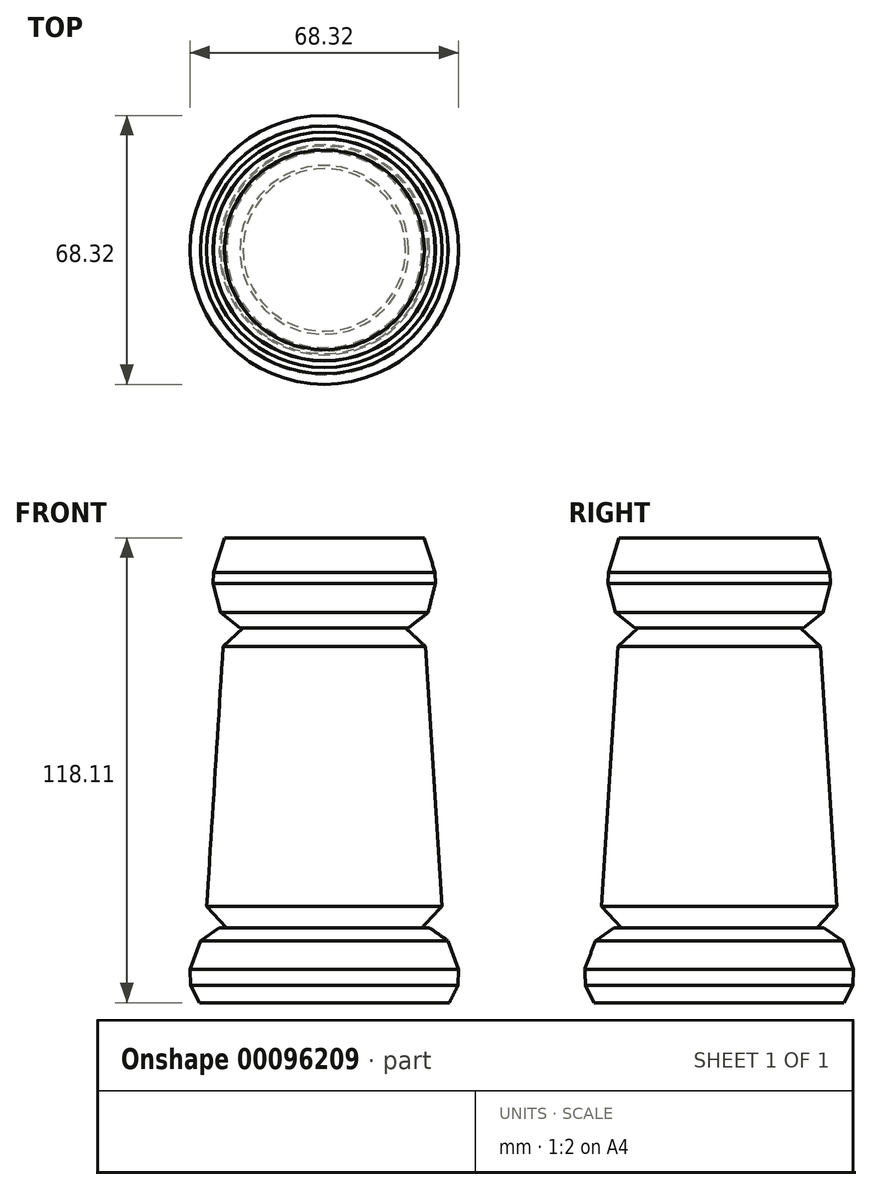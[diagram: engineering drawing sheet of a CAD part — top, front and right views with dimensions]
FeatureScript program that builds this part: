
annotation { "Feature Type Name" : "Feature", "Feature Type Description" : "" }
export const myFeature = defineFeature(function(context is Context, id is Id, definition is map)
    precondition{}
    {
        {
            var Q0;
            Q0=qCreatedBy(makeId("Top.planeOp"),FACE);
            var sketch = newSketch(context, id + "F0", { "sketchPlane" : qUnion([Q0])});
            skCircle(sketch, "E0", {"center": v(0, 0) * mm, "radius": 31.75 * mm});
            skSolve(sketch);
        }
        {
            var Q0;
            Q0=qCreatedBy(makeId("Top.planeOp"),FACE);
            cPlane(context, id + "F1", {"entities" : qUnion([Q0]), "cplaneType" : CPlaneType.OFFSET, "offset" : 6.35 * mm, "width" : 152.4 * mm, "height" : 152.4 * mm});
        }
        {
            var Q0;
            Q0=qCreatedBy(id+"F1.planeOp",FACE);
            var sketch = newSketch(context, id + "F2", { "sketchPlane" : qUnion([Q0])});
            skCircle(sketch, "E1", {"center": v(0, 0) * mm, "radius": 34.92 * mm});
            skSolve(sketch);
        }
        {
            var Q0;
            Q0=makeQuery(id+"F2.imprint","IMPRINT",FACE,{"disambiguationData":[TD([[makeQuery(id+"F2.imprint","IMPRINT",EDGE,{"derivedFrom":sQuery(id+"F2.wireOp",EDGE,"E1")}),1.0]])]});
            var Q1;
            Q1=makeQuery(id+"F0.imprint","IMPRINT",FACE,{"disambiguationData":[TD([[makeQuery(id+"F0.imprint","IMPRINT",EDGE,{"derivedFrom":sQuery(id+"F0.wireOp",EDGE,"E0")}),1.0]])]});
            loft(context, id + "F3", {"sheetProfilesArray" : [{ "sheetProfileEntities" : qUnion([Q0]) }, { "sheetProfileEntities" : qUnion([Q1]) }]});
        }
        {
            var Q0;
            Q0=qCreatedBy(id+"F1.planeOp",FACE);
            cPlane(context, id + "F4", {"entities" : qUnion([Q0]), "cplaneType" : CPlaneType.OFFSET, "offset" : 12.7 * mm, "width" : 152.4 * mm, "height" : 152.4 * mm});
        }
        {
            var Q0;
            Q0=qCreatedBy(id+"F4.planeOp",FACE);
            var sketch = newSketch(context, id + "F5", { "sketchPlane" : qUnion([Q0])});
            skCircle(sketch, "E2", {"center": v(0, 0) * mm, "radius": 30.22 * mm});
            skSolve(sketch);
        }
        {
            var Q1;
            Q1=makeQuery(id+"F5.imprint","IMPRINT",FACE,{"disambiguationData":[TD([[makeQuery(id+"F5.imprint","IMPRINT",EDGE,{"derivedFrom":sQuery(id+"F5.wireOp",EDGE,"E2")}),1.0]])]});
            var Q2;
            Q2=makeQuery(id+"F2.imprint","IMPRINT",FACE,{"disambiguationData":[TD([[makeQuery(id+"F2.imprint","IMPRINT",EDGE,{"derivedFrom":sQuery(id+"F2.wireOp",EDGE,"E1")}),1.0]])]});
            loft(context, id + "F6", {"operationType" : NewBodyOperationType.ADD, "sheetProfilesArray" : [{ "sheetProfileEntities" : qUnion([Q1]) }, { "sheetProfileEntities" : qUnion([Q2]) }]});
        }
        {
            var Q0;
            Q0=qCreatedBy(id+"F4.planeOp",FACE);
            cPlane(context, id + "F7", {"entities" : qUnion([Q0]), "cplaneType" : CPlaneType.OFFSET, "offset" : 76.2 * mm, "width" : 152.4 * mm, "height" : 152.4 * mm});
        }
        {
            var Q0;
            Q0=qCreatedBy(id+"F7.planeOp",FACE);
            var sketch = newSketch(context, id + "F8", { "sketchPlane" : qUnion([Q0])});
            skCircle(sketch, "E3", {"center": v(0, 0) * mm, "radius": 25.4 * mm});
            skSolve(sketch);
        }
        {
            var Q0;
            Q0=qCreatedBy(id+"F7.planeOp",FACE);
            cPlane(context, id + "F9", {"entities" : qUnion([Q0]), "cplaneType" : CPlaneType.OFFSET, "offset" : 12.7 * mm, "width" : 152.4 * mm, "height" : 152.4 * mm});
        }
        {
            var Q0;
            Q0=qCreatedBy(id+"F9.planeOp",FACE);
            var sketch = newSketch(context, id + "F10", { "sketchPlane" : qUnion([Q0])});
            skCircle(sketch, "E4", {"center": v(0, 0) * mm, "radius": 28.58 * mm});
            skSolve(sketch);
        }
        {
            var Q0;
            Q0=makeQuery(id+"F8.imprint","IMPRINT",FACE,{"disambiguationData":[TD([[makeQuery(id+"F8.imprint","IMPRINT",EDGE,{"derivedFrom":sQuery(id+"F8.wireOp",EDGE,"E3")}),1.0]])]});
            var Q1;
            Q1=makeQuery(id+"F10.imprint","IMPRINT",FACE,{"disambiguationData":[TD([[makeQuery(id+"F10.imprint","IMPRINT",EDGE,{"derivedFrom":sQuery(id+"F10.wireOp",EDGE,"E4")}),1.0]])]});
            loft(context, id + "F11", {"sheetProfilesArray" : [{ "sheetProfileEntities" : qUnion([Q0]) }, { "sheetProfileEntities" : qUnion([Q1]) }]});
        }
        {
            var Q0;
            Q0=qCreatedBy(id+"F9.planeOp",FACE);
            cPlane(context, id + "F12", {"entities" : qUnion([Q0]), "cplaneType" : CPlaneType.OFFSET, "offset" : 10.16 * mm, "width" : 152.4 * mm, "height" : 152.4 * mm});
        }
        {
            var Q0;
            Q0=qCreatedBy(id+"F12.planeOp",FACE);
            var sketch = newSketch(context, id + "F13", { "sketchPlane" : qUnion([Q0])});
            skCircle(sketch, "E5", {"center": v(0, 0) * mm, "radius": 25.4 * mm});
            skSolve(sketch);
        }
        {
            var Q0;
            Q0=makeQuery(id+"F6.opLoft","CAP_FACE",FACE,{"disambiguationData":[OSD([makeQuery(id+"F5.imprint","IMPRINT",FACE,{"disambiguationData":[TD([[makeQuery(id+"F5.imprint","IMPRINT",EDGE,{"derivedFrom":sQuery(id+"F5.wireOp",EDGE,"E2")}),1.0]])]})])],"isStart":true});
            var Q1;
            Q1=makeQuery(id+"F11.opLoft","CAP_FACE",FACE,{"disambiguationData":[OSD([makeQuery(id+"F8.imprint","IMPRINT",FACE,{"disambiguationData":[TD([[makeQuery(id+"F8.imprint","IMPRINT",EDGE,{"derivedFrom":sQuery(id+"F8.wireOp",EDGE,"E3")}),1.0]])]})])],"isStart":true});
            loft(context, id + "F14", {"sheetProfilesArray" : [{ "sheetProfileEntities" : qUnion([Q0]) }, { "sheetProfileEntities" : qUnion([Q1]) }]});
        }
        {
            var Q1;
            Q1=makeQuery(id+"F13.imprint","IMPRINT",FACE,{"disambiguationData":[TD([[makeQuery(id+"F13.imprint","IMPRINT",EDGE,{"derivedFrom":sQuery(id+"F13.wireOp",EDGE,"E5")}),1.0]])]});
            var Q2;
            Q2=makeQuery(id+"F11.opLoft","CAP_FACE",FACE,{"disambiguationData":[OSD([makeQuery(id+"F10.imprint","IMPRINT",FACE,{"disambiguationData":[TD([[makeQuery(id+"F10.imprint","IMPRINT",EDGE,{"derivedFrom":sQuery(id+"F10.wireOp",EDGE,"E4")}),1.0]])]})])],"isStart":true});
            loft(context, id + "F15", {"operationType" : NewBodyOperationType.ADD, "sheetProfilesArray" : [{ "sheetProfileEntities" : qUnion([Q1]) }, { "sheetProfileEntities" : qUnion([Q2]) }]});
        }
        {
            var Q0;
            Q0=makeQuery(id+"F14.opLoft","SWEPT_FACE",FACE,{"disambiguationData":[OSD([sQuery(id+"F5.wireOp",EDGE,"E2"),sQuery(id+"F8.wireOp",EDGE,"E3")])]});
            var Q1;
            Q1=makeQuery(id+"F6.opLoft","SWEPT_FACE",FACE,{"disambiguationData":[OSD([sQuery(id+"F2.wireOp",EDGE,"E1"),sQuery(id+"F5.wireOp",EDGE,"E2")])]});
            var Q2;
            Q2=makeQuery(id+"F11.opLoft","SWEPT_FACE",FACE,{"disambiguationData":[OSD([sQuery(id+"F8.wireOp",EDGE,"E3"),sQuery(id+"F10.wireOp",EDGE,"E4")])]});
            chamfer(context, id + "F16", {"entities" : qUnion([Q0, Q1, Q2]), "width" : 5.08 * mm, "tangentPropagation" : true});
        }
    });
